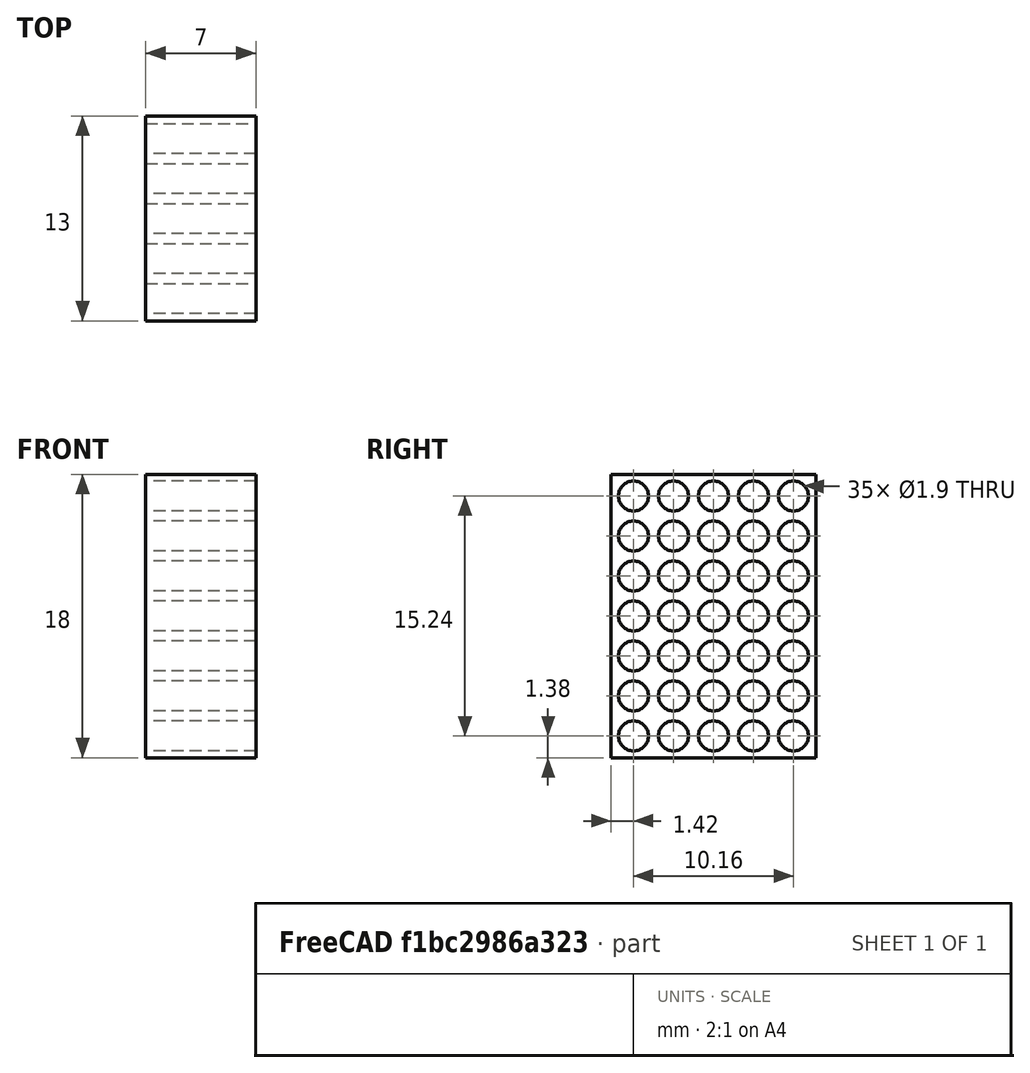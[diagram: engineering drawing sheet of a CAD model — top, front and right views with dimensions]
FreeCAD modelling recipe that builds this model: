
FCSTD DOCUMENT  (FreeCAD 0.14R3702 (Git))
Label: LedMatrix
License: CC-BY 3.0
LicenseURL: http://creativecommons.org/licenses/by/3.0/
objects: Sketcher::SketchObject×1, PartDesign::Pad×1
note: 3 computed .brp shape members not serialized (recipe doc carries the construction recipe); baked Part::Feature solids carry a one-line shape summary decoded from their .brp

FEATURE [Sketcher::SketchObject] Sketch
  Placement = pos=(0,0,0) rot=(0.57735,0.57735,0.57735;2.0944rad)
  sketch-geometry (39):
    g0: LineSegment StartX=0 StartY=0 StartZ=0 EndX=13 EndY=0 EndZ=0
    g1: LineSegment StartX=13 StartY=0 StartZ=0 EndX=13 EndY=18 EndZ=0
    g2: LineSegment StartX=13 StartY=18 StartZ=0 EndX=0 EndY=18 EndZ=0
    g3: LineSegment StartX=0 StartY=18 StartZ=0 EndX=0 EndY=0 EndZ=0
    g4: Circle CenterX=1.42 CenterY=16.62 CenterZ=0 NormalX=0 NormalY=0 NormalZ=1 Radius=0.95
    g5: Circle CenterX=11.58 CenterY=16.62 CenterZ=0 NormalX=0 NormalY=0 NormalZ=1 Radius=0.95
    g6: Circle CenterX=11.58 CenterY=1.38 CenterZ=0 NormalX=0 NormalY=0 NormalZ=1 Radius=0.95
    g7: Circle CenterX=3.96 CenterY=16.62 CenterZ=0 NormalX=0 NormalY=0 NormalZ=1 Radius=0.95
    g8: Circle CenterX=6.5 CenterY=16.62 CenterZ=0 NormalX=0 NormalY=0 NormalZ=1 Radius=0.95
    g9: Circle CenterX=9.04 CenterY=16.62 CenterZ=0 NormalX=0 NormalY=0 NormalZ=1 Radius=0.95
    g10: Circle CenterX=11.58 CenterY=6.46 CenterZ=0 NormalX=0 NormalY=0 NormalZ=1 Radius=0.95
    g11: Circle CenterX=11.58 CenterY=9 CenterZ=0 NormalX=0 NormalY=0 NormalZ=1 Radius=0.95
    g12: Circle CenterX=11.58 CenterY=11.54 CenterZ=0 NormalX=0 NormalY=0 NormalZ=1 Radius=0.95
    g13: Circle CenterX=11.58 CenterY=14.08 CenterZ=0 NormalX=0 NormalY=0 NormalZ=1 Radius=0.95
    g14: Circle CenterX=11.58 CenterY=3.92 CenterZ=0 NormalX=0 NormalY=0 NormalZ=1 Radius=0.95
    g15: Circle CenterX=9.04 CenterY=14.08 CenterZ=0 NormalX=0 NormalY=0 NormalZ=1 Radius=0.95
    g16: Circle CenterX=6.5 CenterY=14.08 CenterZ=0 NormalX=0 NormalY=0 NormalZ=1 Radius=0.95
    g17: Circle CenterX=3.96 CenterY=14.08 CenterZ=0 NormalX=0 NormalY=0 NormalZ=1 Radius=0.95
    g18: Circle CenterX=1.42 CenterY=14.08 CenterZ=0 NormalX=0 NormalY=0 NormalZ=1 Radius=0.95
    g19: Circle CenterX=9.04 CenterY=11.54 CenterZ=0 NormalX=0 NormalY=0 NormalZ=1 Radius=0.95
    g20: Circle CenterX=6.5 CenterY=11.54 CenterZ=0 NormalX=0 NormalY=0 NormalZ=1 Radius=0.95
    g21: Circle CenterX=3.96 CenterY=11.54 CenterZ=0 NormalX=0 NormalY=0 NormalZ=1 Radius=0.95
    g22: Circle CenterX=1.42 CenterY=11.54 CenterZ=0 NormalX=0 NormalY=0 NormalZ=1 Radius=0.95
    g23: Circle CenterX=9.04 CenterY=9 CenterZ=0 NormalX=0 NormalY=0 NormalZ=1 Radius=0.95
    g24: Circle CenterX=6.5 CenterY=9 CenterZ=0 NormalX=0 NormalY=0 NormalZ=1 Radius=0.95
    g25: Circle CenterX=3.96 CenterY=9 CenterZ=0 NormalX=0 NormalY=0 NormalZ=1 Radius=0.95
    g26: Circle CenterX=1.42 CenterY=9 CenterZ=0 NormalX=0 NormalY=0 NormalZ=1 Radius=0.95
    g27: Circle CenterX=9.04 CenterY=6.46 CenterZ=0 NormalX=0 NormalY=0 NormalZ=1 Radius=0.95
    g28: Circle CenterX=6.5 CenterY=6.46 CenterZ=0 NormalX=0 NormalY=0 NormalZ=1 Radius=0.95
    g29: Circle CenterX=3.96 CenterY=6.46 CenterZ=0 NormalX=0 NormalY=0 NormalZ=1 Radius=0.95
    g30: Circle CenterX=1.42 CenterY=6.46 CenterZ=0 NormalX=0 NormalY=0 NormalZ=1 Radius=0.95
    g31: Circle CenterX=1.42 CenterY=3.92 CenterZ=0 NormalX=0 NormalY=0 NormalZ=1 Radius=0.95
    g32: Circle CenterX=3.96 CenterY=3.92 CenterZ=0 NormalX=0 NormalY=0 NormalZ=1 Radius=0.95
    g33: Circle CenterX=6.5 CenterY=3.92 CenterZ=0 NormalX=0 NormalY=0 NormalZ=1 Radius=0.95
    g34: Circle CenterX=9.04 CenterY=3.92 CenterZ=0 NormalX=0 NormalY=0 NormalZ=1 Radius=0.95
    g35: Circle CenterX=9.04 CenterY=1.38 CenterZ=0 NormalX=0 NormalY=0 NormalZ=1 Radius=0.95
    g36: Circle CenterX=6.5 CenterY=1.38 CenterZ=0 NormalX=0 NormalY=0 NormalZ=1 Radius=0.95
    g37: Circle CenterX=3.96 CenterY=1.38 CenterZ=0 NormalX=0 NormalY=0 NormalZ=1 Radius=0.95
    g38: Circle CenterX=1.42 CenterY=1.38 CenterZ=0 NormalX=0 NormalY=0 NormalZ=1 Radius=0.95
  constraints (116):
    c: Coincident(g0,g1)
    c: Coincident(g1,g2)
    c: Coincident(g2,g3)
    c: Coincident(g3,g0)
    c: Horizontal(g0)
    c: Horizontal(g2)
    c: Vertical(g1)
    c: Vertical(g3)
    c: Coincident(g0,g-1)
    c: DistanceX(g-1,g0) = 13
    c: DistanceY(g-1,g2) = 18
    c: Radius(g4) = 0.95
    c: Equal(g5,g4)
    c: DistanceX(g4,g5) = 10.16
    c: DistanceY(g4,g5) = 0
    c: Distance(g4,g3) = 1.42
    c: Equal(g6,g5)
    c: DistanceY(g6,g5) = 15.24
    c: Distance(g6,g0) = 1.38
    c: DistanceX(g6,g5) = 0
    c: DistanceX(g7,g4) = -2.54
    c: Equal(g7,g4)
    c: DistanceY(g7,g4) = 0
    c: Equal(g8,g7)
    c: DistanceX(g8,g7) = -2.54
    c: DistanceY(g8,g7) = 0
    c: Equal(g9,g8)
    c: DistanceX(g9,g8) = -2.54
    c: DistanceY(g9,g8) = 0
    c: Equal(g6,g14)
    c: Equal(g14,g10)
    c: Equal(g10,g11)
    c: Equal(g11,g12)
    c: Equal(g12,g13)
    c: DistanceX(g14,g6) = 0
    c: DistanceY(g6,g14) = 2.54
    c: DistanceY(g10,g14) = -2.54
    c: DistanceY(g11,g10) = -2.54
    c: DistanceY(g12,g11) = -2.54
    c: DistanceY(g12,g13) = 2.54
    c: DistanceX(g14,g10) = 0
    c: DistanceX(g10,g11) = 0
    c: DistanceX(g11,g12) = 0
    c: DistanceX(g13,g12) = 0
    c: Equal(g13,g15)
    c: Equal(g15,g16)
    c: Equal(g16,g17)
    c: Equal(g17,g18)
    c: DistanceX(g15,g9) = 0
    c: DistanceY(g15,g13) = 0
    c: DistanceX(g16,g8) = 0
    c: DistanceY(g15,g16) = 0
    c: DistanceY(g17,g16) = 0
    c: DistanceX(g7,g17) = 0
    c: DistanceY(g18,g17) = 0
    c: DistanceX(g18,g4) = 0
    c: Equal(g12,g19)
    c: Equal(g19,g20)
    c: Equal(g20,g21)
    c: Equal(g21,g22)
    c: DistanceY(g12,g19) = 0
    c: DistanceY(g19,g20) = 0
    c: DistanceY(g20,g21) = 0
    c: DistanceY(g22,g21) = 0
    c: DistanceX(g19,g15) = 0
    c: DistanceX(g16,g20) = 0
    c: DistanceX(g21,g17) = 0
    c: DistanceX(g22,g18) = 0
    c: Equal(g11,g23)
    c: Equal(g23,g24)
    c: Equal(g24,g25)
    c: Equal(g25,g26)
    c: DistanceY(g11,g23) = 0
    c: DistanceY(g23,g24) = 0
    c: DistanceY(g24,g25) = 0
    c: DistanceY(g26,g25) = 0
    c: DistanceX(g23,g19) = 0
    c: DistanceX(g24,g20) = 0
    c: DistanceX(g25,g21) = 0
    c: DistanceX(g26,g22) = 0
    c: DistanceY(g35,g6) = 0
    c: DistanceY(g35,g36) = 0
    c: DistanceY(g36,g37) = 0
    c: DistanceY(g37,g38) = 0
    c: DistanceY(g34,g14) = 0
    c: DistanceY(g33,g34) = 0
    c: DistanceY(g32,g33) = 0
    c: DistanceY(g31,g32) = 0
    c: DistanceY(g27,g10) = 0
    c: DistanceY(g28,g27) = 0
    c: DistanceY(g29,g28) = 0
    c: DistanceY(g30,g29) = 0
    c: DistanceX(g27,g23) = 0
    c: DistanceX(g28,g24) = 0
    c: DistanceX(g29,g25) = 0
    c: DistanceX(g30,g26) = 0
    c: DistanceX(g34,g27) = 0
    c: DistanceX(g33,g28) = 0
    c: DistanceX(g32,g29) = 0
    c: DistanceX(g31,g30) = 0
    c: DistanceX(g35,g34) = 0
    c: DistanceX(g36,g33) = 0
    c: DistanceX(g37,g32) = 0
    c: DistanceX(g38,g31) = 0
    c: Equal(g6,g35)
    c: Equal(g35,g34)
    c: Equal(g34,g27)
    c: Equal(g27,g28)
    c: Equal(g28,g33)
    c: Equal(g33,g36)
    c: Equal(g36,g37)
    c: Equal(g37,g32)
    c: Equal(g32,g29)
    c: Equal(g29,g30)
    c: Equal(g30,g31)
    c: Equal(g31,g38)
FEATURE [PartDesign::Pad] Pad  label="led_7x5"
  Length = 7
  Length2 = 100
  Placement = pos=(0,0,0) rot=(0.57735,0.57735,0.57735;2.0944rad)
  Sketch = -> Sketch
  Type = 0
